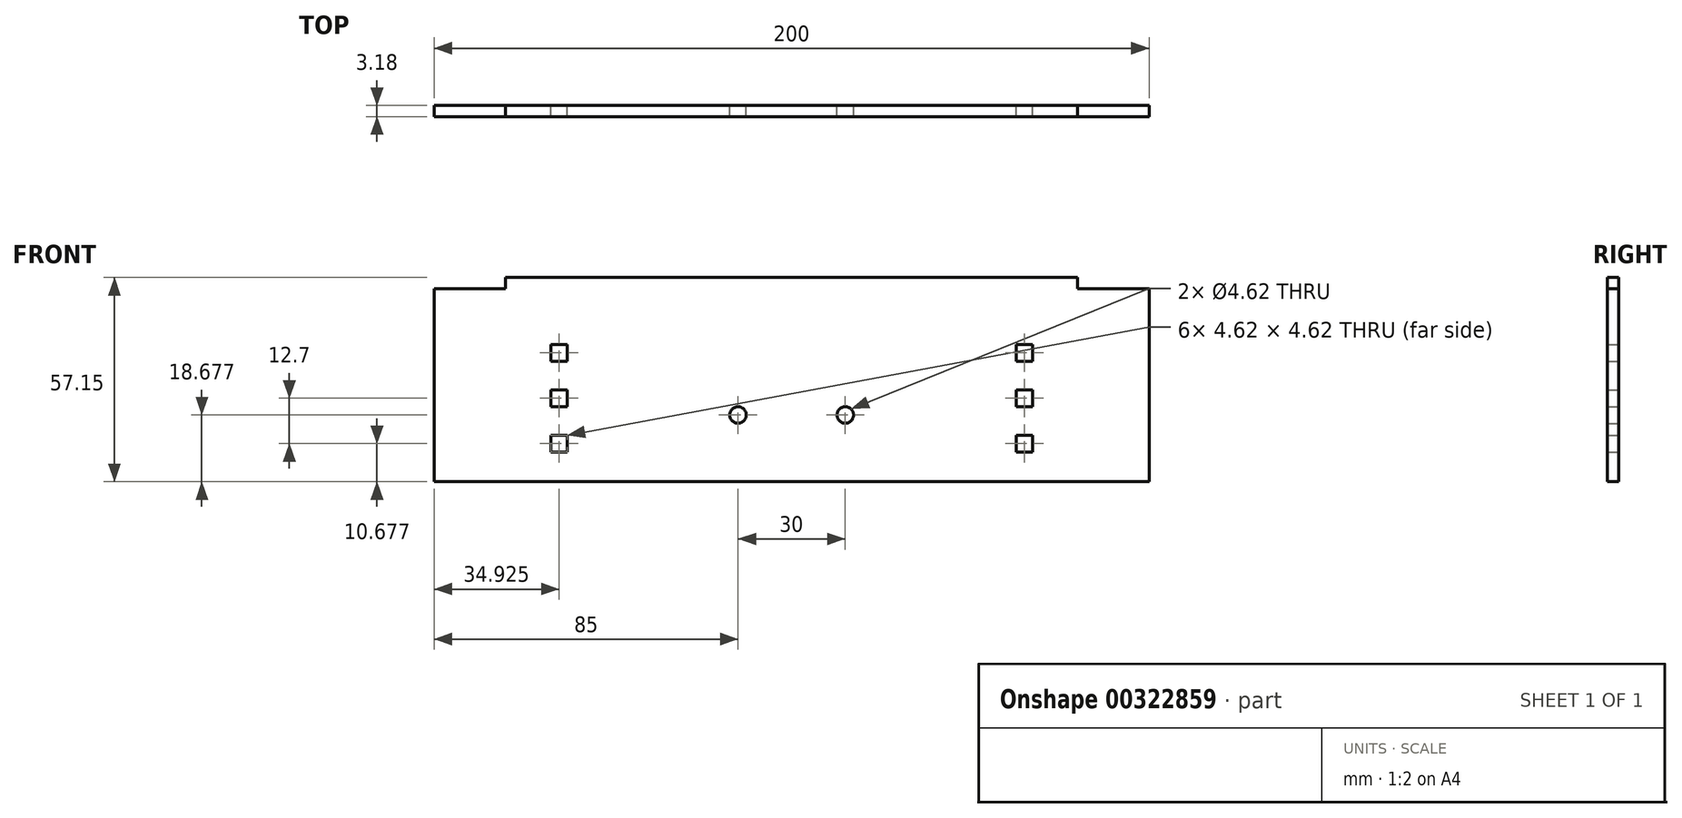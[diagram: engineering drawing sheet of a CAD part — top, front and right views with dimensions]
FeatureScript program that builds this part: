
annotation { "Feature Type Name" : "Feature", "Feature Type Description" : "" }
export const myFeature = defineFeature(function(context is Context, id is Id, definition is map)
    precondition{}
    {
        {
            var Q0;
            Q0=qCreatedBy(makeId("Front.planeOp"),FACE);
            var sketch = newSketch(context, id + "F0", { "sketchPlane" : qUnion([Q0])});
            skLineSegment(sketch, "E0.bottom", {"start": v(100, 26.99) * mm, "end": v(80, 26.99) * mm});
            skLineSegment(sketch, "E0.top", {"start": v(100, -26.99) * mm, "end": v(-100, -26.99) * mm});
            skLineSegment(sketch, "E0.left", {"start": v(100, 26.99) * mm, "end": v(100, -26.99) * mm});
            skLineSegment(sketch, "E0.right", {"start": v(-100, 26.99) * mm, "end": v(-100, -26.99) * mm});
            skPoint(sketch, "E0.middle", {"position": v(0, 0) * mm});
            skLineSegment(sketch, "E1", {"start": v(-100, -26.99) * mm, "end": v(-65.07, -26.99) * mm});
            skLineSegment(sketch, "E2.bottom", {"start": v(-62.76, -18.62) * mm, "end": v(-67.39, -18.62) * mm});
            skLineSegment(sketch, "E2.top", {"start": v(-62.76, -14) * mm, "end": v(-67.39, -14) * mm});
            skLineSegment(sketch, "E2.left", {"start": v(-62.76, -18.62) * mm, "end": v(-62.76, -14) * mm});
            skLineSegment(sketch, "E2.right", {"start": v(-67.39, -18.62) * mm, "end": v(-67.39, -14) * mm});
            skPoint(sketch, "E2.middle", {"position": v(-65.07, -16.31) * mm});
            skLineSegment(sketch, "E3.0.1.0", {"start": v(-62.76, -5.92) * mm, "end": v(-62.76, -1.3) * mm});
            skLineSegment(sketch, "E3.0.1.1", {"start": v(-62.76, -5.92) * mm, "end": v(-67.39, -5.92) * mm});
            skLineSegment(sketch, "E3.0.1.2", {"start": v(-67.39, -5.92) * mm, "end": v(-67.39, -1.3) * mm});
            skLineSegment(sketch, "E3.0.1.3", {"start": v(-62.76, -1.3) * mm, "end": v(-67.39, -1.3) * mm});
            skLineSegment(sketch, "E3.0.2.0", {"start": v(-62.76, 6.78) * mm, "end": v(-62.76, 11.4) * mm});
            skLineSegment(sketch, "E3.0.2.1", {"start": v(-62.76, 6.78) * mm, "end": v(-67.39, 6.78) * mm});
            skLineSegment(sketch, "E3.0.2.2", {"start": v(-67.39, 6.78) * mm, "end": v(-67.39, 11.4) * mm});
            skLineSegment(sketch, "E3.0.2.3", {"start": v(-62.76, 11.4) * mm, "end": v(-67.39, 11.4) * mm});
            skLineSegment(sketch, "E3.direction2", {"start": v(-62.76, -18.62) * mm, "end": v(-62.76, -14) * mm, "construction": true});
            skLineSegment(sketch, "E4.top", {"start": v(80, 30.16) * mm, "end": v(-80, 30.16) * mm});
            skLineSegment(sketch, "E4.left", {"start": v(80, 26.99) * mm, "end": v(80, 30.16) * mm});
            skLineSegment(sketch, "E4.right", {"start": v(-80, 26.99) * mm, "end": v(-80, 30.16) * mm});
            skPoint(sketch, "E4.middle", {"position": v(0, 26.99) * mm});
            skPoint(sketch, "E4.bottom.start.orphan", {"position": v(80, 23.81) * mm});
            skLineSegment(sketch, "E5.trimOffspring", {"start": v(-80, 26.99) * mm, "end": v(-100, 26.99) * mm});
            skPoint(sketch, "E6.orphan", {"position": v(-80, 23.81) * mm});
            skLineSegment(sketch, "E7", {"start": v(0, -26.99) * mm, "end": v(0, 30.16) * mm});
            skPoint(sketch, "E8.MirrorP", {"position": v(65.07, -16.31) * mm});
            skLineSegment(sketch, "E9.MirrorCS", {"start": v(62.76, -18.62) * mm, "end": v(67.39, -18.62) * mm});
            skLineSegment(sketch, "E10.MirrorCS", {"start": v(62.76, -18.62) * mm, "end": v(62.76, -14) * mm});
            skLineSegment(sketch, "E11.MirrorCS", {"start": v(62.76, -14) * mm, "end": v(67.39, -14) * mm});
            skLineSegment(sketch, "E12.MirrorCS", {"start": v(67.39, -18.62) * mm, "end": v(67.39, -14) * mm});
            skLineSegment(sketch, "E13.MirrorCS", {"start": v(67.39, 6.78) * mm, "end": v(67.39, 11.4) * mm});
            skLineSegment(sketch, "E14.MirrorCS", {"start": v(62.76, 6.78) * mm, "end": v(67.39, 6.78) * mm});
            skLineSegment(sketch, "E15.MirrorCS", {"start": v(62.76, 6.78) * mm, "end": v(62.76, 11.4) * mm});
            skLineSegment(sketch, "E16.MirrorCS", {"start": v(62.76, 11.4) * mm, "end": v(67.39, 11.4) * mm});
            skLineSegment(sketch, "E17.MirrorCS", {"start": v(62.76, -18.62) * mm, "end": v(62.76, -14) * mm, "construction": true});
            skLineSegment(sketch, "E18.MirrorCS", {"start": v(62.76, -5.92) * mm, "end": v(62.76, -1.3) * mm});
            skLineSegment(sketch, "E19.MirrorCS", {"start": v(62.76, -1.3) * mm, "end": v(67.39, -1.3) * mm});
            skLineSegment(sketch, "E20.MirrorCS", {"start": v(67.39, -5.92) * mm, "end": v(67.39, -1.3) * mm});
            skLineSegment(sketch, "E21.MirrorCS", {"start": v(62.76, -5.92) * mm, "end": v(67.39, -5.92) * mm});
            skLineSegment(sketch, "E22", {"start": v(0, -26.99) * mm, "end": v(0, -8.31) * mm});
            skLineSegment(sketch, "E23", {"start": v(0, -8.31) * mm, "end": v(15, -8.31) * mm});
            skCircle(sketch, "E24", {"center": v(15, -8.31) * mm, "radius": 2.31 * mm});
            skCircle(sketch, "E25.MirrorC", {"center": v(-15, -8.31) * mm, "radius": 2.31 * mm});
            skSolve(sketch);
        }
        {
            var Q0;
            Q0 = qSketchRegion(id + "F0", true);
            extrude(context, id + "F1", {"entities" : qUnion([Q0]), "depth" : 3.17 * mm});
        }
    });
